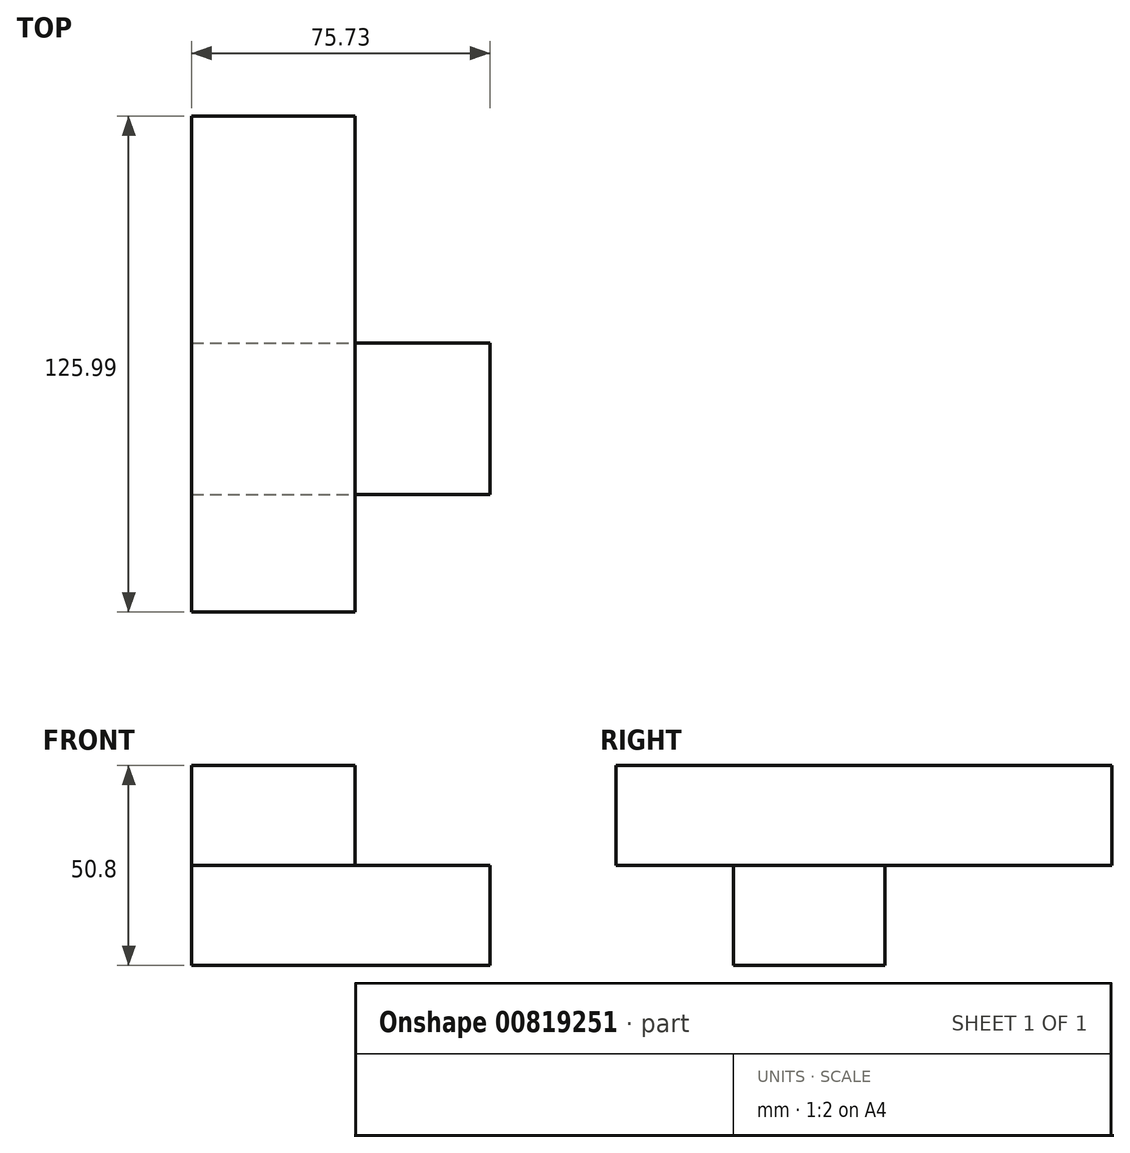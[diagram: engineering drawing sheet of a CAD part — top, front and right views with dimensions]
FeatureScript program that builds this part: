
annotation { "Feature Type Name" : "Feature", "Feature Type Description" : "" }
export const myFeature = defineFeature(function(context is Context, id is Id, definition is map)
    precondition{}
    {
        {
            var Q0;
            Q0=qCreatedBy(makeId("Top.planeOp"),FACE);
            var sketch = newSketch(context, id + "F0", { "sketchPlane" : qUnion([Q0])});
            skLineSegment(sketch, "E0.bottom", {"start": v(0, 0) * mm, "end": v(75.73, 0) * mm});
            skLineSegment(sketch, "E0.top", {"start": v(0, -38.48) * mm, "end": v(75.73, -38.48) * mm});
            skLineSegment(sketch, "E0.left", {"start": v(0, 0) * mm, "end": v(0, -38.48) * mm});
            skLineSegment(sketch, "E0.right", {"start": v(75.73, 0) * mm, "end": v(75.73, -38.48) * mm});
            skSolve(sketch);
        }
        {
            var Q0;
            Q0=makeQuery(id+"F0.imprint","IMPRINT",FACE,{"disambiguationData":[TD([[makeQuery(id+"F0.imprint","IMPRINT",EDGE,{"derivedFrom":sQuery(id+"F0.wireOp",EDGE,"E0.bottom")}),-1.0]])]});
            extrude(context, id + "F1", {"entities" : qUnion([Q0]), "depth" : 25.4 * mm, "offsetDistance" : 25.4 * mm});
        }
        {
            var Q0;
            Q0=makeQuery(id+"F1.opExtrude","CAP_FACE",FACE,{"disambiguationData":[OSD([sQuery(id+"F0.wireOp",EDGE,"E0.bottom"),sQuery(id+"F0.wireOp",EDGE,"E0.top"),sQuery(id+"F0.wireOp",EDGE,"E0.left"),sQuery(id+"F0.wireOp",EDGE,"E0.right")])],"isStart":false});
            var sketch = newSketch(context, id + "F2", { "sketchPlane" : qUnion([Q0])});
            skLineSegment(sketch, "E1.bottom", {"start": v(0, -68.35) * mm, "end": v(41.53, -68.35) * mm});
            skLineSegment(sketch, "E1.top", {"start": v(0, 57.64) * mm, "end": v(41.53, 57.64) * mm});
            skLineSegment(sketch, "E1.left", {"start": v(0, -68.35) * mm, "end": v(0, 57.64) * mm});
            skLineSegment(sketch, "E1.right", {"start": v(41.53, -68.35) * mm, "end": v(41.53, 57.64) * mm});
            skSolve(sketch);
        }
        {
            var Q0;
            {var subQ0=sQuery(id+"F2.wireOp",EDGE,"E1.top");Q0=makeQuery(id+"F2.imprint","IMPRINT",FACE,{"disambiguationData":[TD([[makeQuery(id+"F2.imprint","IMPRINT",EDGE,{"derivedFrom":subQ0}),-1.0]])]});}
            var Q1;
            {var subQ0=sQuery(id+"F2.wireOp",EDGE,"E1.bottom");Q1=makeQuery(id+"F2.imprint","IMPRINT",FACE,{"disambiguationData":[TD([[makeQuery(id+"F2.imprint","IMPRINT",EDGE,{"derivedFrom":subQ0}),1.0]])]});}
            var Q2;
            {var subQ0=sQuery(id+"F2.wireOp",EDGE,"E1.left");var subQ1=makeQuery(id+"F1.opExtrude","CAP_EDGE",EDGE,{"disambiguationData":[OSD([sQuery(id+"F0.wireOp",EDGE,"E0.bottom")])],"isStart":false});var subQ2=makeQuery(id+"F2.imprint","INTERSECT",VERTEX,{"derivedFrom":[subQ1,subQ0]});var subQ3=makeQuery(id+"F1.opExtrude","CAP_EDGE",EDGE,{"disambiguationData":[OSD([sQuery(id+"F0.wireOp",EDGE,"E0.top")])],"isStart":false});var subQ4=makeQuery(id+"F2.imprint","INTERSECT",VERTEX,{"derivedFrom":[subQ3,subQ0]});Q2=makeQuery(id+"F2.imprint","IMPRINT",FACE,{"disambiguationData":[TD([[makeQuery(id+"F2.imprint","IMPRINT",EDGE,{"disambiguationData":[TD([[subQ2,-1.0],[subQ4,1.0]])],"derivedFrom":subQ0}),1.0]])]});}
            extrude(context, id + "F3", {"entities" : qUnion([Q0, Q1, Q2]), "operationType" : NewBodyOperationType.ADD, "depth" : 25.4 * mm, "offsetDistance" : 25.4 * mm});
        }
    });
